# Revit family: BIMLIB_Уголок_с_настенным_креплением ВР_PEX_РОСТерм
name_source: partatom
category: Соединительные детали трубопроводов
revit_build: Autodesk Revit 2017 (Build: 20170118_1100(x64)
units: mm (PartAtom-declared; Revit-internal decimal feet)

## family parameters
Всегда вертикально = Да
На основе рабочей плоскости = Нет
Общий = Нет
При загрузке вырезать с полостями = Нет
Размер круглого соединителя = Использовать диаметр
Тип детали = Отвод

## types (1)
- BIMLIB_Уголок_с_настенным_креплением ВР_PEX_РОСТерм
    ADSK_URL документации изделия = http://rostherm.ru
    ADSK_URL страницы изделия = http://rostherm.ru
    ADSK_Версия Revit = 2017
    ADSK_Единица измерения = шт.
    ADSK_Завод-изготовитель = РОСТерм
    ADSK_Материал = BIMLIB_Медь_РТ
    ADSK_Обозначение = ГОСТ 32415-2013
    BL_BIM library = https://bimlib.pro
    URL = http://rostherm.ru
    Изготовитель = РОСТерм
    Описание = Уголок с настенным креплением ВР PEX
    РТ_DN2 = 15 мм

## geometry (parser evidence)
native form markers: Sweep x2
no freeform markers — native parametric forms only
